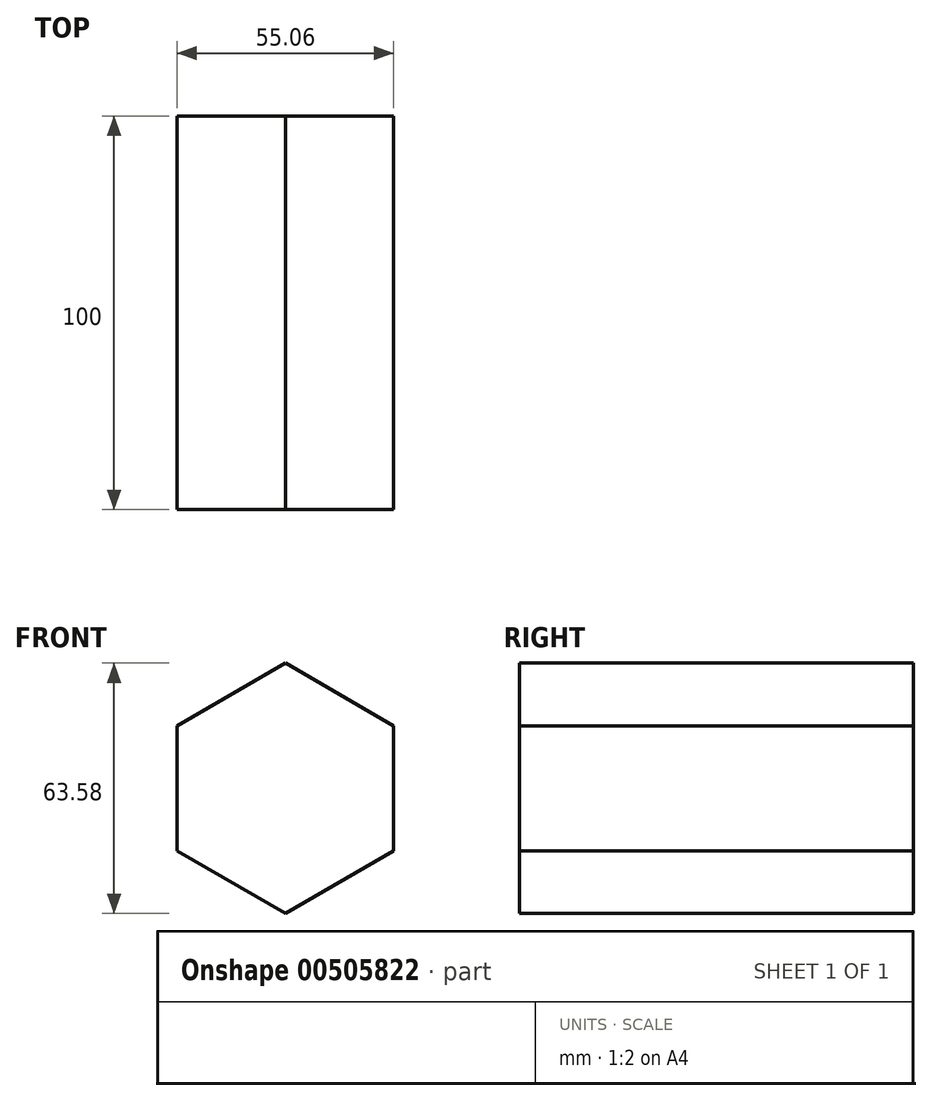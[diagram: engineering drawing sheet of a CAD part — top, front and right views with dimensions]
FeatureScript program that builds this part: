
annotation { "Feature Type Name" : "Feature", "Feature Type Description" : "" }
export const myFeature = defineFeature(function(context is Context, id is Id, definition is map)
    precondition{}
    {
        {
            var Q0;
            Q0=qCreatedBy(makeId("Front.planeOp"),FACE);
            var sketch = newSketch(context, id + "F0", { "sketchPlane" : qUnion([Q0])});
            skCircle(sketch, "E0.cCircle", {"center": v(0, 0) * mm, "radius": 27.53 * mm, "construction": true});
            skLineSegment(sketch, "E0.0", {"start": v(-27.53, -15.9) * mm, "end": v(-27.53, 15.9) * mm});
            skLineSegment(sketch, "E0.1", {"start": v(-27.53, 15.9) * mm, "end": v(0, 31.8) * mm});
            skLineSegment(sketch, "E0.2", {"start": v(0, 31.8) * mm, "end": v(27.53, 15.9) * mm});
            skLineSegment(sketch, "E0.3", {"start": v(27.53, 15.9) * mm, "end": v(27.53, -15.9) * mm});
            skLineSegment(sketch, "E0.4", {"start": v(27.53, -15.9) * mm, "end": v(0, -31.8) * mm});
            skLineSegment(sketch, "E0.5", {"start": v(0, -31.8) * mm, "end": v(-27.53, -15.9) * mm});
            skPoint(sketch, "E0.0.midPoint", {"position": v(-27.53, 0) * mm});
            skSolve(sketch);
        }
        {
            var Q0;
            Q0 = qSketchRegion(id + "F0", true);
            extrude(context, id + "F1", {"entities" : qUnion([Q0]), "endBound" : BoundingType.SYMMETRIC, "depth" : 100 * mm});
        }
    });
